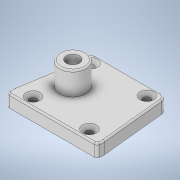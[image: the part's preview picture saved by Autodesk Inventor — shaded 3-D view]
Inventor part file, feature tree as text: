
AUTODESK INVENTOR PART (.ipt)
format: ipt  version: 2020.3 (Build 243373000, 373)  size: 357,376 bytes
history: native  units: mm
features: sketch x3, extrude x3, hole x3, fillet x2
ambient origin geometry x8: Origin, YZ Plane, XZ Plane, XY Plane, X Axis, Y Axis, Z Axis, Center Point
bodies: Body1 (feature_tree)
feature tree (11):
  sketch  "Sketch1"  dims[d0=135.0deg d4=24.6mm]
  extrude  "Extrusion12"  Depth=24.6mm
  extrude  "Extrusion13"  Depth=70.0mm
  extrude  "Extrusion14"  Depth=6.5mm
  hole  "Hole3"  [1 undecoded]
  fillet  "Fillet10"  Radius=6.0mm
  fillet  "Fillet11"  Radius=2.0mm
  hole  "Hole4"  [1 undecoded]
  hole  "Hole5"  [1 undecoded]
  sketch  "Sketch2"  dims[d5=12.4mm d6=70.0mm]
  sketch  "Sketch4"  dims[d7=60.0mm d9=8.5mm d10=135.0deg d12=6.0mm d13=2.0mm d14=2.0mm d16=20.0mm d23=5.0mm d29=130.0mm d32=15.0mm d33=4.0mm d34=28.4mm d38=4.0mm d40=6.8mm d49=30.0mm d50=84.0mm d51=3.0mm d52=3.0mm d53=1.5mm d54=20.0mm d59=1.0mm d60=90.0mm d61=135.0deg d70=135.0deg d82=0.7mm d83=0.7mm d84=0.7mm d85=0.7mm d86=6.0mm d102=18.0mm d103=4.0mm d104=0.0mm d105=4.0mm d106=0.0mm d107=11.4mm d108=0.0mm d116=4.2mm d117=6.0mm d118=5.6mm d119=0.85mm d120=90.0deg d121=4.2mm d122=0.0mm d123=2.0mm d125=0.5mm d126=2.0mm d128=1.0mm d135=2.3mm d136=6.0mm d137=4.5mm d138=2.0mm d139=90.0deg d140=6.5mm d141=0.0mm d142=5.6mm d143=6.0mm d144=9.0mm d145=1.0mm d146=90.0deg d147=6.5mm d148=0.0mm]
note: 3 required parameter values undecoded (feature->parameter linkage not recoverable at this tier; creation-order binding heuristic only, values carry confidence <= 0.55)
